# Revit family: Dali 500W Dimmer_455
name_source: partatom
category: Electrical Fixtures
revit_build: Autodesk Revit 2018 (Build: 20170223_1515(x64)
units: mm (PartAtom-declared; Revit-internal decimal feet)

## family parameters
Always vertical = Yes
Cut with Voids When Loaded = No
Maintain Annotation Orientation = No
OmniClass Number = 23.80.00.00
OmniClass Title = Electric Power and Lighting
Part Type = Normal
Room Calculation Point = No
Round Connector Dimension = Use Diameter
Shared = No
Work Plane-Based = Yes

## types (1)
- DIGIDIM 500W Thyristor Dimmer
    Ambient temperature = 0 °C to + 40 °C
    DALI : = Standard DIGIDIM removable terminal block 0.5 mm² – 1.5 mm²
stranded or solid core
    DALI consumption = 2 mA
    Dali supply = None (Use external DALI power supply)
    Default Elevation = 0 mm  [stored 0 ft]
    Dimensions: = 35 mm × 90 mm × 58 mm
    EMC emission = EN 55015
    EMC immunity = EN 61547
    Environment = Complies with WEEE and RoHS
directives.
    Heat dissipation = 3.5 W with maximum load (resistive)
    Housing = DIN-rail case 35 mm wide
    IP code: = IP30
    Isolation = 3 kV
    Mains Supply = 220 VAC – 240 VAC, 50 Hz – 60 Hz
    Mains: = Up to 4 mm² solid core or up to 2.5 mm² stranded
Note: If equipment is used in an
electrically noisy environment, the
DALI cable should be screened and connected to the earth
    Manufacturer = Helvar
    Model = 455
    Mounting = DIN rail (installation in switchgear/ controlgear cabinet)
    Relative humidity = Max. 90 %, noncondensing
    Safety = EN 61347-2-11
    Storage temperature = −10 °C to + 70 °C
    Weight: = 110g

note: [stored X ft] marks values corroborated as IEEE doubles in the binary element streams (Revit-internal decimal feet)

## geometry (parser evidence)
native form markers: Sweep x3
no freeform markers — native parametric forms only
